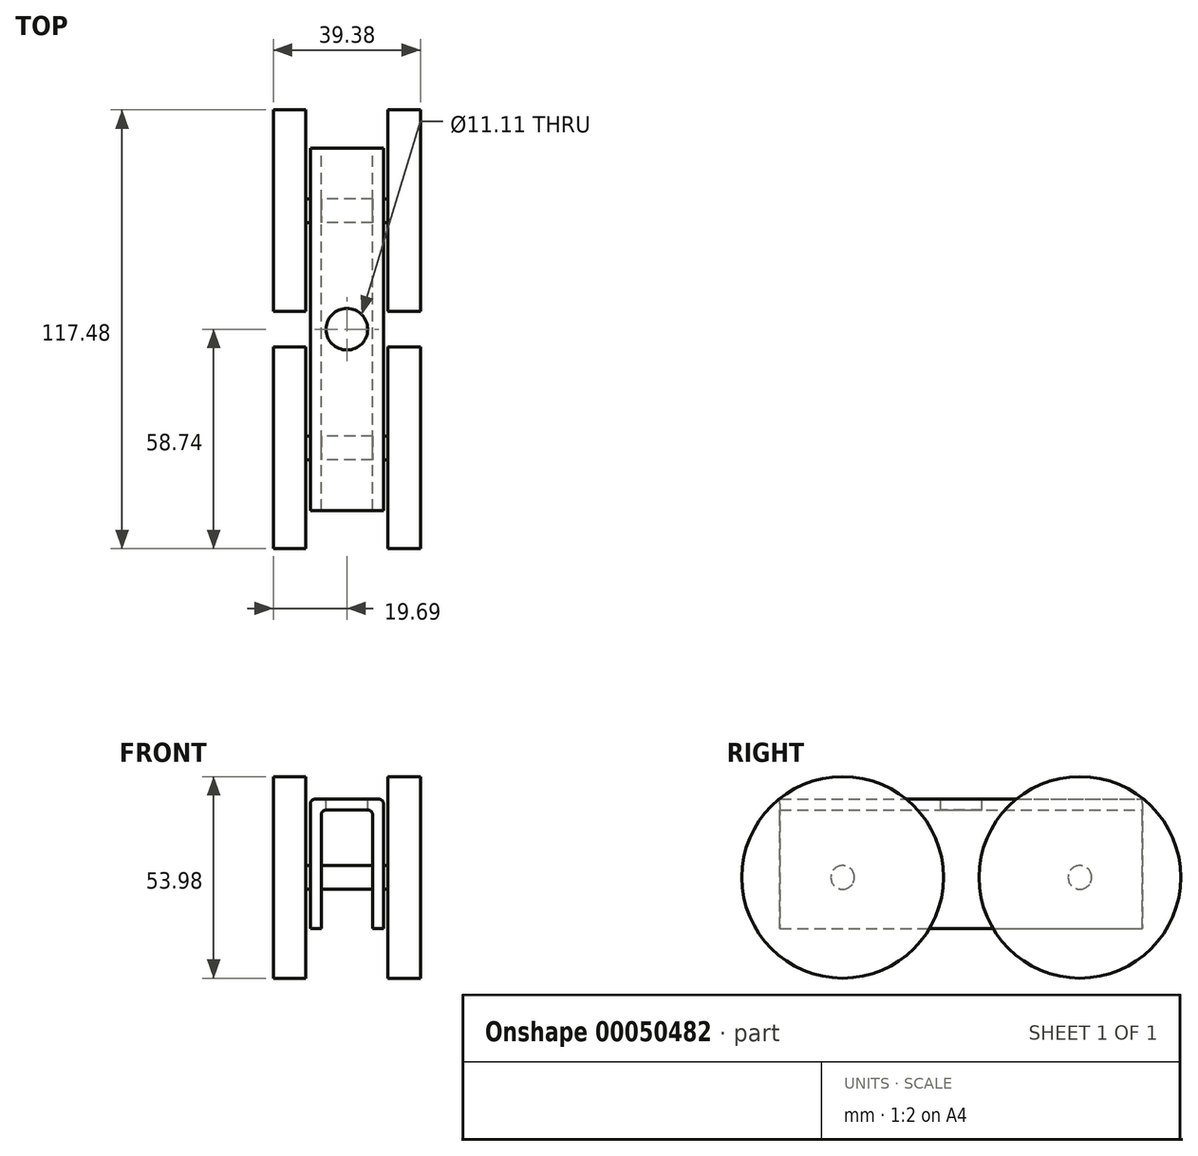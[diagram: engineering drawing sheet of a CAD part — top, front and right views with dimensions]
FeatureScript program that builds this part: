
annotation { "Feature Type Name" : "Feature", "Feature Type Description" : "" }
export const myFeature = defineFeature(function(context is Context, id is Id, definition is map)
    precondition{}
    {
        {
            var Q0;
            Q0=qCreatedBy(makeId("Front.planeOp"),FACE);
            var sketch = newSketch(context, id + "F0", { "sketchPlane" : qUnion([Q0])});
            skLineSegment(sketch, "E0.rect.bottom", {"start": v(8.5, 17.34) * mm, "end": v(-8.5, 17.34) * mm});
            skLineSegment(sketch, "E0.rect.top", {"start": v(9.78, -17.34) * mm, "end": v(6.86, -17.34) * mm});
            skLineSegment(sketch, "E0.rect.left", {"start": v(9.78, 16.07) * mm, "end": v(9.78, -17.34) * mm});
            skLineSegment(sketch, "E0.rect.right", {"start": v(-9.78, 16.07) * mm, "end": v(-9.78, -17.34) * mm});
            skPoint(sketch, "E0.rect.middle", {"position": v(0, 0) * mm});
            skLineSegment(sketch, "E1.top", {"start": v(-5.59, 14.41) * mm, "end": v(5.59, 14.41) * mm});
            skLineSegment(sketch, "E1.left", {"start": v(-6.86, -17.34) * mm, "end": v(-6.86, 13.14) * mm});
            skLineSegment(sketch, "E1.right", {"start": v(6.86, -17.34) * mm, "end": v(6.86, 13.14) * mm});
            skLineSegment(sketch, "E2.trimOffspring", {"start": v(-6.86, -17.34) * mm, "end": v(-9.78, -17.34) * mm});
            skLineSegment(sketch, "E3", {"start": v(0, 14.41) * mm, "end": v(0, 17.34) * mm, "construction": true});
            skPoint(sketch, "E4.visualSharp", {"position": v(-6.86, 14.41) * mm});
            skArc(sketch, "E4.filletArc", {"start": v(-5.59, 14.41) * mm, "mid": v(-6.49, 14.04) * mm, "end": v(-6.86, 13.14) * mm});
            skPoint(sketch, "E5.visualSharp", {"position": v(6.86, 14.41) * mm});
            skArc(sketch, "E5.filletArc", {"start": v(6.86, 13.14) * mm, "mid": v(6.49, 14.04) * mm, "end": v(5.59, 14.41) * mm});
            skPoint(sketch, "E6.visualSharp", {"position": v(9.78, 17.34) * mm});
            skArc(sketch, "E6.filletArc", {"start": v(9.78, 16.07) * mm, "mid": v(9.4, 16.96) * mm, "end": v(8.5, 17.34) * mm});
            skPoint(sketch, "E7.visualSharp", {"position": v(-9.78, 17.34) * mm});
            skArc(sketch, "E7.filletArc", {"start": v(-8.5, 17.34) * mm, "mid": v(-9.4, 16.96) * mm, "end": v(-9.78, 16.07) * mm});
            skSolve(sketch);
        }
        {
            var Q0;
            Q0 = qSketchRegion(id + "F0", true);
            extrude(context, id + "F1", {"entities" : qUnion([Q0]), "endBound" : BoundingType.SYMMETRIC, "depth" : 97.03 * mm});
        }
        {
            var Q0;
            Q0=makeQuery(id+"F1.opExtrude","SWEPT_FACE",FACE,{"disambiguationData":[OSD([sQuery(id+"F0.wireOp",EDGE,"E0.rect.left")])]});
            var sketch = newSketch(context, id + "F2", { "sketchPlane" : qUnion([Q0])});
            skCircle(sketch, "E8", {"center": v(-31.75, -3.62) * mm, "radius": 3.18 * mm});
            skCircle(sketch, "E9", {"center": v(31.75, -3.62) * mm, "radius": 3.18 * mm});
            skLineSegment(sketch, "E10", {"start": v(-31.75, -3.62) * mm, "end": v(0, 0) * mm, "construction": true});
            skLineSegment(sketch, "E11", {"start": v(0, 0) * mm, "end": v(31.75, -3.62) * mm, "construction": true});
            skSolve(sketch);
        }
        {
            var Q0;
            Q0 = qSketchRegion(id + "F2", true);
            var Q1;
            Q1=makeQuery(id+"F1.opExtrude","SWEPT_FACE",FACE,{"disambiguationData":[OSD([sQuery(id+"F0.wireOp",EDGE,"E0.rect.right")])]});
            extrude(context, id + "F3", {"entities" : qUnion([Q0]), "operationType" : NewBodyOperationType.REMOVE, "endBound" : BoundingType.UP_TO_SURFACE, "oppositeDirection" : true, "endBoundEntityFace" : qUnion([Q1]), "depth" : 25.4 * mm});
        }
        {
            var Q0;
            Q0=qCreatedBy(makeId("Right.planeOp"),FACE);
            var sketch = newSketch(context, id + "F4", { "sketchPlane" : qUnion([Q0])});
            skCircle(sketch, "E12", {"center": v(-31.75, -3.62) * mm, "radius": 3.18 * mm});
            skCircle(sketch, "E13", {"center": v(31.75, -3.62) * mm, "radius": 3.18 * mm});
            skSolve(sketch);
        }
        {
            var Q0;
            Q0 = qSketchRegion(id + "F4", true);
            extrude(context, id + "F5", {"entities" : qUnion([Q0]), "operationType" : NewBodyOperationType.ADD, "endBound" : BoundingType.SYMMETRIC, "depth" : 39.37 * mm});
        }
        {
            var Q0;
            Q0=makeQuery(id+"F5.opExtrude","CAP_FACE",FACE,{"disambiguationData":[OSD([sQuery(id+"F4.wireOp",EDGE,"E12")])],"isStart":false});
            var sketch = newSketch(context, id + "F6", { "sketchPlane" : qUnion([Q0])});
            skCircle(sketch, "E14", {"center": v(-31.75, -3.62) * mm, "radius": 26.99 * mm});
            skCircle(sketch, "E15", {"center": v(31.75, -3.62) * mm, "radius": 26.99 * mm});
            skSolve(sketch);
        }
        {
            var Q0;
            Q0 = qSketchRegion(id + "F6", true);
            extrude(context, id + "F7", {"entities" : qUnion([Q0]), "operationType" : NewBodyOperationType.ADD, "oppositeDirection" : true, "depth" : 8.7 * mm});
        }
        {
            var Q0;
            Q0=makeQuery(id+"F1.opExtrude","SWEPT_BODY",BODY,{"disambiguationData":[OSD([sQuery(id+"F0.wireOp",EDGE,"E0.rect.bottom"),sQuery(id+"F0.wireOp",EDGE,"E0.rect.top"),sQuery(id+"F0.wireOp",EDGE,"E0.rect.left"),sQuery(id+"F0.wireOp",EDGE,"E0.rect.right"),sQuery(id+"F0.wireOp",EDGE,"E1.top"),sQuery(id+"F0.wireOp",EDGE,"E1.left"),sQuery(id+"F0.wireOp",EDGE,"E1.right"),sQuery(id+"F0.wireOp",EDGE,"E2.trimOffspring"),sQuery(id+"F0.wireOp",EDGE,"E4.filletArc"),sQuery(id+"F0.wireOp",EDGE,"E5.filletArc"),sQuery(id+"F0.wireOp",EDGE,"E6.filletArc"),sQuery(id+"F0.wireOp",EDGE,"E7.filletArc")])]});
            var Q1;
            Q1=qCreatedBy(makeId("Right.planeOp"),FACE);
            mirror(context, id + "F8", {"operationType" : NewBodyOperationType.ADD, "entities" : qUnion([Q0]), "mirrorPlane" : qUnion([Q1])});
        }
        {
            var Q0;
            Q0=makeQuery(id+"F1.opExtrude","SWEPT_FACE",FACE,{"disambiguationData":[OSD([sQuery(id+"F0.wireOp",EDGE,"E0.rect.bottom")])]});
            var sketch = newSketch(context, id + "F9", { "sketchPlane" : qUnion([Q0])});
            skCircle(sketch, "E16", {"center": v(0, 0) * mm, "radius": 5.56 * mm});
            skSolve(sketch);
        }
        {
            var Q0;
            Q0 = qSketchRegion(id + "F9", true);
            extrude(context, id + "F10", {"entities" : qUnion([Q0]), "operationType" : NewBodyOperationType.REMOVE, "endBound" : BoundingType.UP_TO_NEXT, "oppositeDirection" : true, "depth" : 25.4 * mm});
        }
    });
